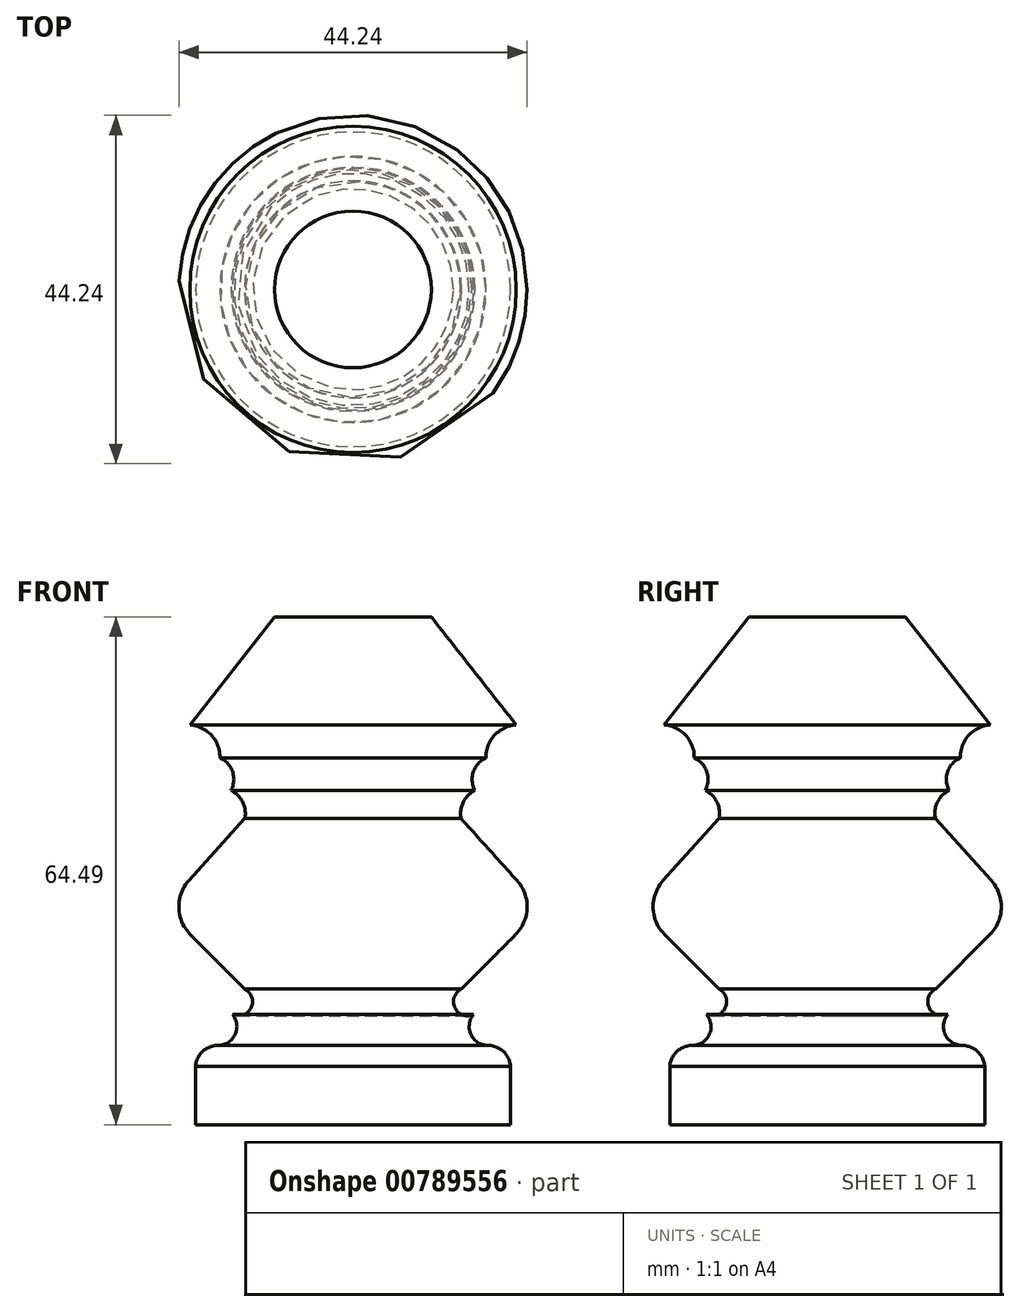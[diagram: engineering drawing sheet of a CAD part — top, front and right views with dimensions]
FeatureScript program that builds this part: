
annotation { "Feature Type Name" : "Feature", "Feature Type Description" : "" }
export const myFeature = defineFeature(function(context is Context, id is Id, definition is map)
    precondition{}
    {
        {
            var Q0;
            Q0=qCreatedBy(makeId("Front.planeOp"),FACE);
            var sketch = newSketch(context, id + "F0", { "sketchPlane" : qUnion([Q0])});
            skLineSegment(sketch, "E0.bottom", {"start": v(0, 0) * mm, "end": v(20, 0) * mm});
            skLineSegment(sketch, "E0.right", {"start": v(20, 0) * mm, "end": v(20, 7.4) * mm});
            skLineSegment(sketch, "E1.top", {"start": v(0, 64.49) * mm, "end": v(9.95, 64.49) * mm});
            skLineSegment(sketch, "E1.right", {"start": v(20.72, 50.79) * mm, "end": v(9.95, 64.49) * mm});
            skLineSegment(sketch, "E2", {"start": v(20.84, 31) * mm, "end": v(13.75, 38.87) * mm});
            skLineSegment(sketch, "E3", {"start": v(20.67, 24.16) * mm, "end": v(13.78, 17.23) * mm});
            skPoint(sketch, "E4.orphan", {"position": v(24, 41) * mm});
            skPoint(sketch, "E5.orphan", {"position": v(24, 14.01) * mm});
            skArc(sketch, "E6", {"start": v(16.9, 46.58) * mm, "mid": v(15.3, 44.82) * mm, "end": v(15.5, 42.46) * mm});
            skArc(sketch, "E7", {"start": v(20.72, 50.79) * mm, "mid": v(17.97, 49.45) * mm, "end": v(16.9, 46.58) * mm});
            skArc(sketch, "E8", {"start": v(15.5, 42.46) * mm, "mid": v(14, 40.97) * mm, "end": v(13.75, 38.87) * mm});
            skArc(sketch, "E9", {"start": v(13.78, 17.23) * mm, "mid": v(12.94, 14.85) * mm, "end": v(15.33, 14.01) * mm});
            skArc(sketch, "E10", {"start": v(15.33, 14.01) * mm, "mid": v(14.98, 11.46) * mm, "end": v(17.15, 10.07) * mm});
            skArc(sketch, "E11", {"start": v(20, 7.4) * mm, "mid": v(19.1, 9.3) * mm, "end": v(17.15, 10.07) * mm});
            skPoint(sketch, "E12.visualSharp", {"position": v(24, 27.5) * mm});
            skArc(sketch, "E12.filletArc", {"start": v(20.67, 24.16) * mm, "mid": v(22.12, 27.55) * mm, "end": v(20.84, 31) * mm});
            skLineSegment(sketch, "E13", {"start": v(0, 64.49) * mm, "end": v(0, 0) * mm});
            skSolve(sketch);
        }
        {
            var Q0;
            Q0=makeQuery(id+"F0.imprint","IMPRINT",FACE,{"disambiguationData":[TD([[makeQuery(id+"F0.imprint","IMPRINT",EDGE,{"derivedFrom":sQuery(id+"F0.wireOp",EDGE,"E0.bottom")}),1.0]])]});
            var Q1;
            Q1=sQuery(id+"F0.wireOp",EDGE,"E13");
            revolve(context, id + "F1", {"surfaceOperationType" : NewSurfaceOperationType.NEW, "entities" : qUnion([Q0]), "axis" : qUnion([Q1]), "revolveType" : RevolveType.FULL});
        }
    });
